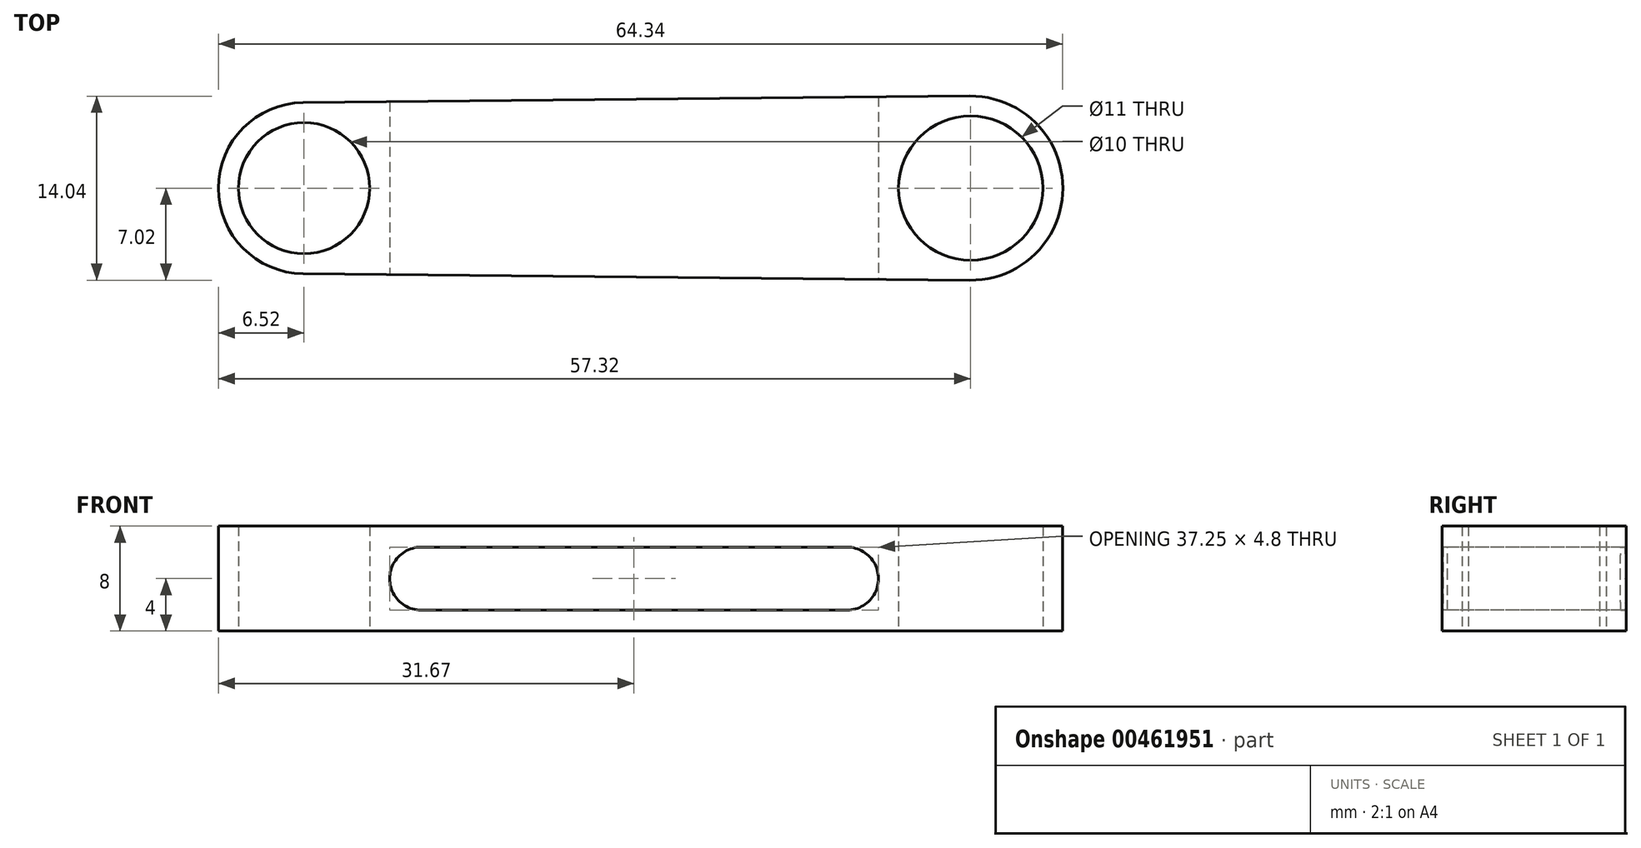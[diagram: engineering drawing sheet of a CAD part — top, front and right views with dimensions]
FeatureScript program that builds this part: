
annotation { "Feature Type Name" : "Feature", "Feature Type Description" : "" }
export const myFeature = defineFeature(function(context is Context, id is Id, definition is map)
    precondition{}
    {
        {
            var Q0;
            Q0=qCreatedBy(makeId("Top.planeOp"),FACE);
            var sketch = newSketch(context, id + "F0", { "sketchPlane" : qUnion([Q0])});
            skCircle(sketch, "E0", {"center": v(25.4, 0) * mm, "radius": 5.5 * mm});
            skCircle(sketch, "E1", {"center": v(-25.4, 0) * mm, "radius": 5 * mm});
            skCircle(sketch, "E2.0", {"center": v(-25.4, 0) * mm, "radius": 6.52 * mm});
            skCircle(sketch, "E3.0", {"center": v(25.4, 0) * mm, "radius": 7.02 * mm});
            skLineSegment(sketch, "E4", {"start": v(-25.46, 6.52) * mm, "end": v(25.33, 7.02) * mm});
            skLineSegment(sketch, "E5", {"start": v(-25.46, -6.52) * mm, "end": v(25.33, -7.02) * mm});
            skSolve(sketch);
        }
        {
            assignVariable(context, id + "F1", {"name" : "rod_thk", "anyValue" : 8 * mm});
        }
        {
            var Q0;
            {var subQ0=sQuery(id+"F0.wireOp",EDGE,"E4");Q0=makeQuery(id+"F0.imprint","IMPRINT",FACE,{"disambiguationData":[TD([[makeQuery(id+"F0.imprint","IMPRINT",EDGE,{"derivedFrom":subQ0}),-1.0]])]});}
            var Q1;
            Q1=makeQuery(id+"F0.imprint","IMPRINT",FACE,{"disambiguationData":[TD([[makeQuery(id+"F0.imprint","IMPRINT",EDGE,{"derivedFrom":sQuery(id+"F0.wireOp",EDGE,"E0")}),-1.0]])]});
            var Q2;
            Q2=makeQuery(id+"F0.imprint","IMPRINT",FACE,{"disambiguationData":[TD([[makeQuery(id+"F0.imprint","IMPRINT",EDGE,{"derivedFrom":sQuery(id+"F0.wireOp",EDGE,"E1")}),-1.0]])]});
            extrude(context, id + "F2", {"entities" : qUnion([Q0, Q1, Q2]), "depth" : getVariable(context, 'rod_thk'), "symmetric" : true});
        }
        {
            var Q0;
            Q0=qCreatedBy(makeId("Front.planeOp"),FACE);
            var sketch = newSketch(context, id + "F3", { "sketchPlane" : qUnion([Q0])});
            skLineSegment(sketch, "E6", {"start": v(-20.4, 4) * mm, "end": v(-20.4, -4) * mm});
            skLineSegment(sketch, "E7", {"start": v(-30.4, -4) * mm, "end": v(-30.4, 4) * mm});
            skLineSegment(sketch, "E8", {"start": v(30.9, 4) * mm, "end": v(30.9, -4) * mm});
            skLineSegment(sketch, "E9", {"start": v(19.9, -4) * mm, "end": v(19.9, 4) * mm});
            skLineSegment(sketch, "E10.bottom", {"start": v(18.38, 2.4) * mm, "end": v(-18.88, 2.4) * mm});
            skLineSegment(sketch, "E10.top", {"start": v(18.38, -2.4) * mm, "end": v(-18.88, -2.4) * mm});
            skLineSegment(sketch, "E10.left", {"start": v(18.38, 2.4) * mm, "end": v(18.38, -2.4) * mm});
            skLineSegment(sketch, "E10.right", {"start": v(-18.88, 2.4) * mm, "end": v(-18.88, -2.4) * mm});
            skPoint(sketch, "E10.middle", {"position": v(-0.25, 0) * mm});
            skSolve(sketch);
        }
        {
            var Q0;
            Q0 = qSketchRegion(id + "F3", true);
            extrude(context, id + "F4", {"entities" : qUnion([Q0]), "operationType" : NewBodyOperationType.REMOVE, "endBound" : BoundingType.THROUGH_ALL, "oppositeDirection" : true, "depth" : 25.4 * mm, "hasSecondDirection" : true, "secondDirectionBound" : BoundingType.THROUGH_ALL, "secondDirectionOppositeDirection" : false, "secondDirectionDepth" : 25.4 * mm});
        }
        {
            var Q0;
            Q0=makeQuery(id+"F4.boolean.opBoolean","COPY",EDGE,{"derivedFrom":makeQuery(id+"F4.opExtrude","SWEPT_EDGE",EDGE,{"disambiguationData":[OSD([sQuery(id+"F3.wireOp",EDGE,"E10.bottom"),sQuery(id+"F3.wireOp",EDGE,"E10.right")])]})});
            var Q1;
            Q1=makeQuery(id+"F4.boolean.opBoolean","COPY",EDGE,{"derivedFrom":makeQuery(id+"F4.opExtrude","SWEPT_EDGE",EDGE,{"disambiguationData":[OSD([sQuery(id+"F3.wireOp",EDGE,"E10.top"),sQuery(id+"F3.wireOp",EDGE,"E10.right")])]})});
            var Q2;
            Q2=makeQuery(id+"F4.boolean.opBoolean","COPY",EDGE,{"derivedFrom":makeQuery(id+"F4.opExtrude","SWEPT_EDGE",EDGE,{"disambiguationData":[OSD([sQuery(id+"F3.wireOp",EDGE,"E10.top"),sQuery(id+"F3.wireOp",EDGE,"E10.left")])]})});
            var Q3;
            Q3=makeQuery(id+"F4.boolean.opBoolean","COPY",EDGE,{"derivedFrom":makeQuery(id+"F4.opExtrude","SWEPT_EDGE",EDGE,{"disambiguationData":[OSD([sQuery(id+"F3.wireOp",EDGE,"E10.bottom"),sQuery(id+"F3.wireOp",EDGE,"E10.left")])]})});
            fillet(context, id + "F5", {"entities" : qUnion([Q0, Q1, Q2, Q3]), "radius" : 2.4 * mm, "tangentPropagation" : true, "allowEdgeOverflow" : false});
        }
    });
